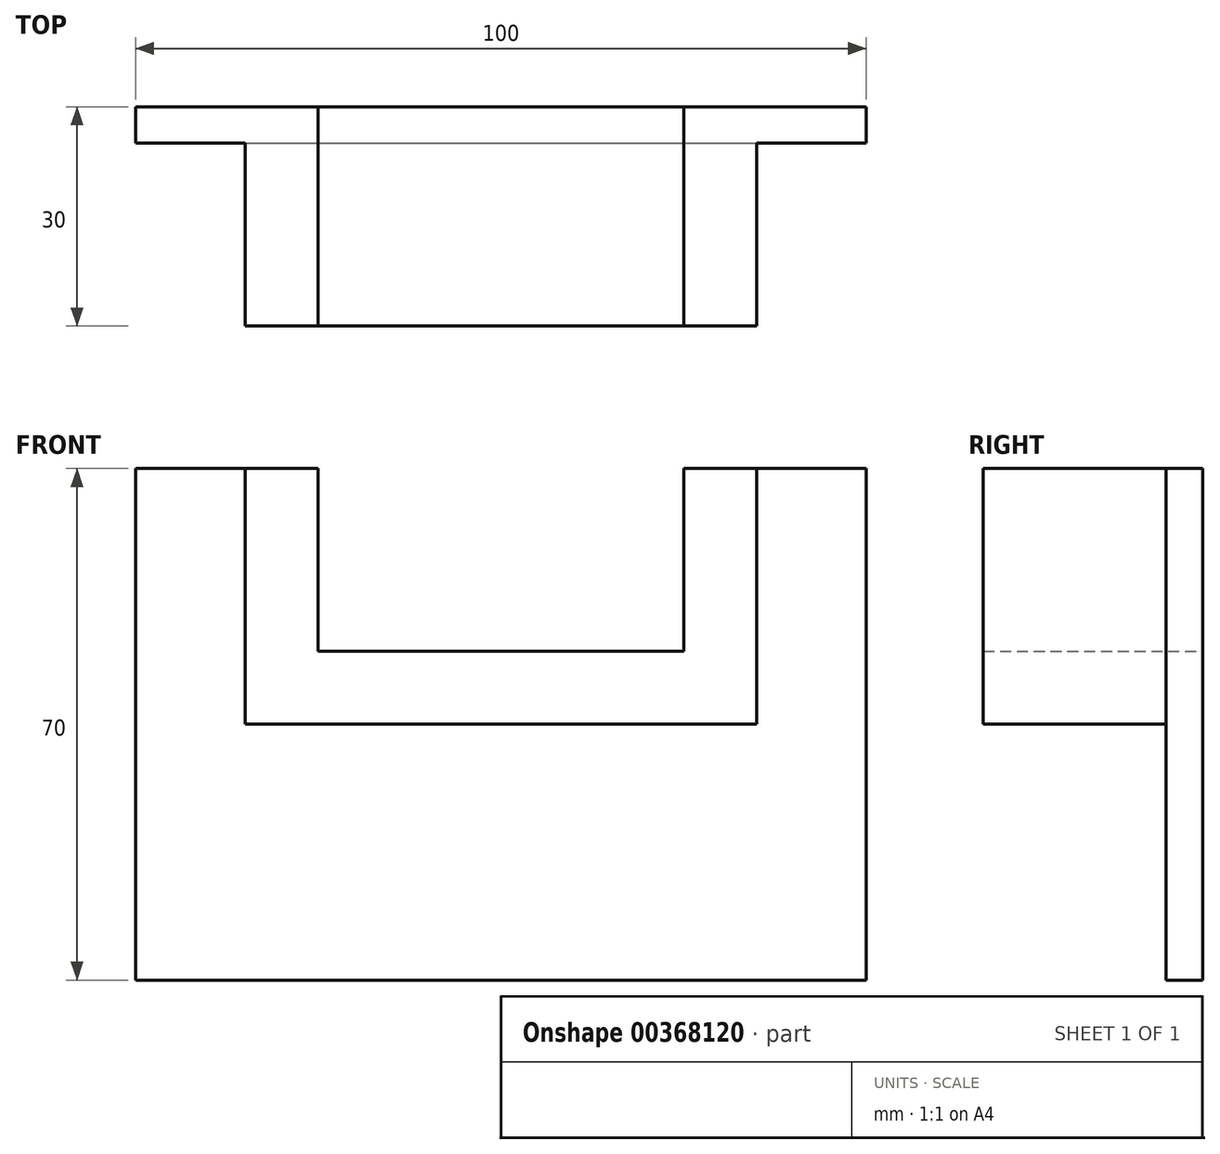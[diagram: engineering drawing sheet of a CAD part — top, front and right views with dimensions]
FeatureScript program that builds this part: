
annotation { "Feature Type Name" : "Feature", "Feature Type Description" : "" }
export const myFeature = defineFeature(function(context is Context, id is Id, definition is map)
    precondition{}
    {
        {
            var Q0;
            Q0=qCreatedBy(makeId("Front.planeOp"),FACE);
            var sketch = newSketch(context, id + "F0", { "sketchPlane" : qUnion([Q0])});
            skLineSegment(sketch, "E0", {"start": v(25, 10) * mm, "end": v(25, 35) * mm});
            skLineSegment(sketch, "E1", {"start": v(25, 35) * mm, "end": v(50, 35) * mm});
            skLineSegment(sketch, "E2", {"start": v(50, 35) * mm, "end": v(50, -35) * mm});
            skLineSegment(sketch, "E3.MirrorCS", {"start": v(-50, 35) * mm, "end": v(-50, -35) * mm});
            skLineSegment(sketch, "E4.MirrorCS", {"start": v(-25, 10) * mm, "end": v(-25, 35) * mm});
            skLineSegment(sketch, "E5.MirrorCS", {"start": v(-25, 35) * mm, "end": v(-50, 35) * mm});
            skLineSegment(sketch, "E6", {"start": v(-50, -35) * mm, "end": v(50, -35) * mm});
            skLineSegment(sketch, "E7", {"start": v(25, 10) * mm, "end": v(-25, 10) * mm});
            skLineSegment(sketch, "E8", {"start": v(-35, 0) * mm, "end": v(35, 0) * mm});
            skLineSegment(sketch, "E9", {"start": v(35, 0) * mm, "end": v(35, 35) * mm});
            skLineSegment(sketch, "E10", {"start": v(-35, 0) * mm, "end": v(-35, 35) * mm});
            skSolve(sketch);
        }
        {
            var Q0;
            {var subQ4=sQuery(id+"F0.wireOp",EDGE,"E0");Q0=makeQuery(id+"F0.imprint","IMPRINT",FACE,{"disambiguationData":[TD([[makeQuery(id+"F0.imprint","IMPRINT",EDGE,{"derivedFrom":subQ4}),-1.0]])]});}
            extrude(context, id + "F1", {"entities" : qUnion([Q0]), "depth" : 30 * mm});
        }
        {
            var Q0;
            {var subQ1=sQuery(id+"F0.wireOp",EDGE,"E2");Q0=makeQuery(id+"F0.imprint","IMPRINT",FACE,{"disambiguationData":[TD([[makeQuery(id+"F0.imprint","IMPRINT",EDGE,{"derivedFrom":subQ1}),-1.0]])]});}
            extrude(context, id + "F2", {"entities" : qUnion([Q0]), "operationType" : NewBodyOperationType.ADD, "depth" : 5 * mm});
        }
    });
